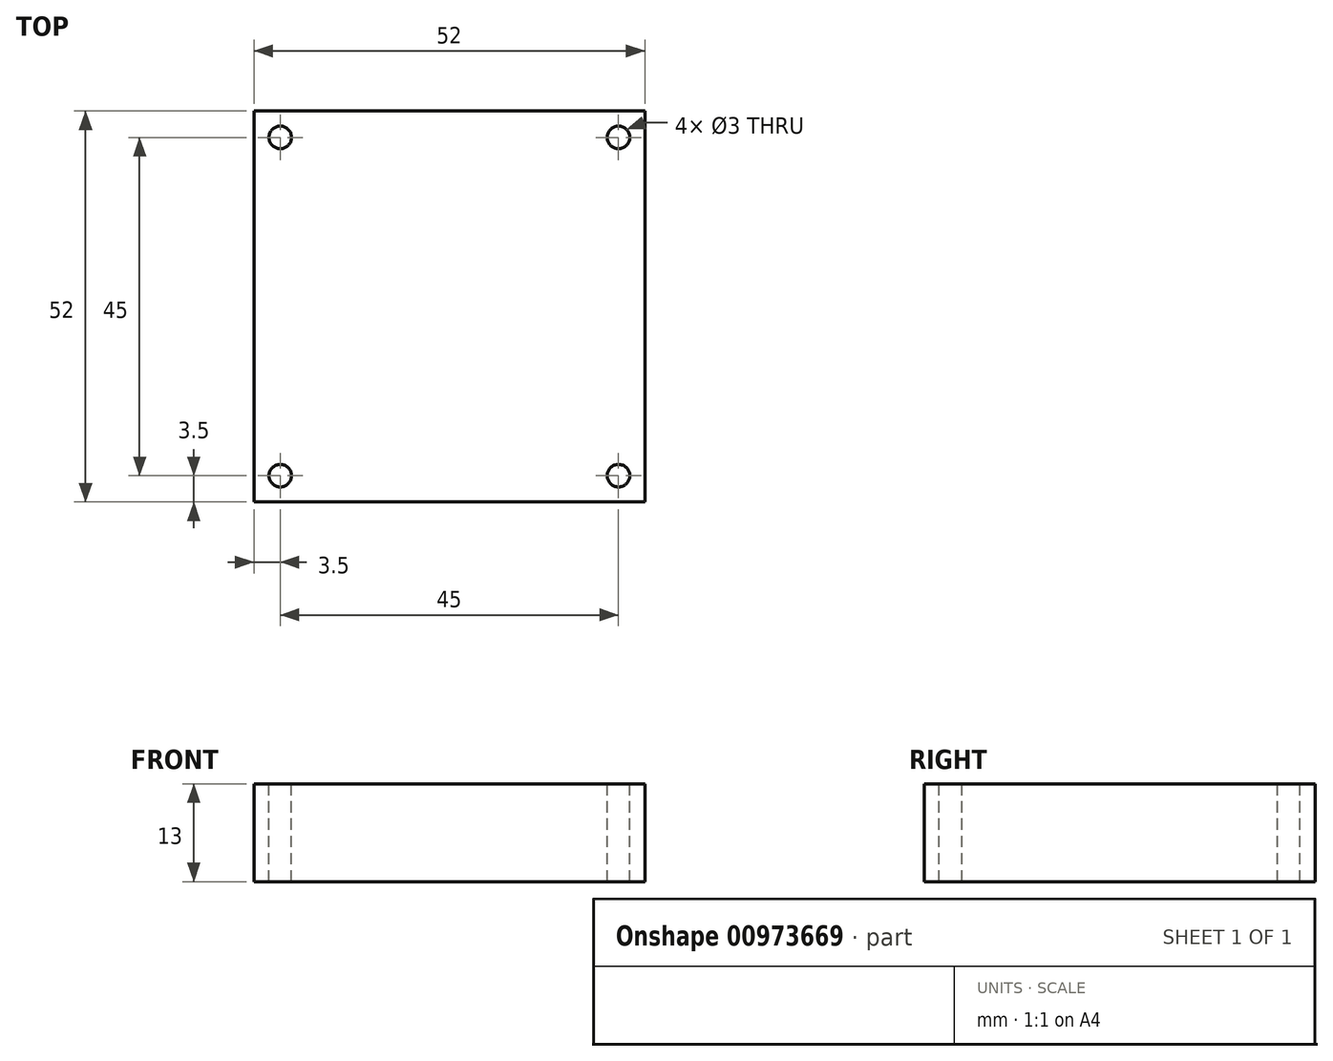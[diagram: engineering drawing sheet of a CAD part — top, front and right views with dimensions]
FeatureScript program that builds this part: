
annotation { "Feature Type Name" : "Feature", "Feature Type Description" : "" }
export const myFeature = defineFeature(function(context is Context, id is Id, definition is map)
    precondition{}
    {
        {
            var Q0;
            Q0=qCreatedBy(makeId("Top.planeOp"),FACE);
            var sketch = newSketch(context, id + "F0", { "sketchPlane" : qUnion([Q0])});
            skLineSegment(sketch, "E0.bottom", {"start": v(-26, 26) * mm, "end": v(26, 26) * mm});
            skLineSegment(sketch, "E0.top", {"start": v(-26, -26) * mm, "end": v(26, -26) * mm});
            skLineSegment(sketch, "E0.left", {"start": v(-26, 26) * mm, "end": v(-26, -26) * mm});
            skLineSegment(sketch, "E0.right", {"start": v(26, 26) * mm, "end": v(26, -26) * mm});
            skPoint(sketch, "E0.middle", {"position": v(0, 0) * mm});
            skSolve(sketch);
        }
        {
            var Q0;
            Q0 = qSketchRegion(id + "F0", true);
            extrude(context, id + "F1", {"entities" : qUnion([Q0]), "depth" : 13 * mm, "offsetDistance" : 25 * mm});
        }
        {
            var Q0;
            Q0=makeQuery(id+"F1.opExtrude","CAP_FACE",FACE,{"disambiguationData":[OSD([sQuery(id+"F0.wireOp",EDGE,"E0.bottom"),sQuery(id+"F0.wireOp",EDGE,"E0.top"),sQuery(id+"F0.wireOp",EDGE,"E0.left"),sQuery(id+"F0.wireOp",EDGE,"E0.right")])],"isStart":false});
            var sketch = newSketch(context, id + "F2", { "sketchPlane" : qUnion([Q0])});
            skCircle(sketch, "E1", {"center": v(-22.5, 22.5) * mm, "radius": 1.5 * mm});
            skCircle(sketch, "E2", {"center": v(22.5, 22.5) * mm, "radius": 1.5 * mm});
            skCircle(sketch, "E3", {"center": v(-22.5, -22.5) * mm, "radius": 1.5 * mm});
            skCircle(sketch, "E4", {"center": v(22.5, -22.5) * mm, "radius": 1.5 * mm});
            skLineSegment(sketch, "E5", {"start": v(-22.5, 22.5) * mm, "end": v(22.5, 22.5) * mm, "construction": true});
            skLineSegment(sketch, "E6", {"start": v(22.5, 22.5) * mm, "end": v(22.5, -22.5) * mm, "construction": true});
            skLineSegment(sketch, "E7", {"start": v(-22.5, -22.5) * mm, "end": v(22.5, -22.5) * mm, "construction": true});
            skLineSegment(sketch, "E8", {"start": v(-22.5, -22.5) * mm, "end": v(-22.5, 22.5) * mm, "construction": true});
            skLineSegment(sketch, "E9", {"start": v(-22.5, 22.5) * mm, "end": v(22.5, -22.5) * mm, "construction": true});
            skSolve(sketch);
        }
        {
            var Q0;
            Q0=makeQuery(id+"F2.imprint","IMPRINT",FACE,{"disambiguationData":[TD([[makeQuery(id+"F2.imprint","IMPRINT",EDGE,{"derivedFrom":sQuery(id+"F2.wireOp",EDGE,"E3")}),1.0]])]});
            var Q1;
            Q1=makeQuery(id+"F2.imprint","IMPRINT",FACE,{"disambiguationData":[TD([[makeQuery(id+"F2.imprint","IMPRINT",EDGE,{"derivedFrom":sQuery(id+"F2.wireOp",EDGE,"E4")}),1.0]])]});
            var Q2;
            Q2=makeQuery(id+"F2.imprint","IMPRINT",FACE,{"disambiguationData":[TD([[makeQuery(id+"F2.imprint","IMPRINT",EDGE,{"derivedFrom":sQuery(id+"F2.wireOp",EDGE,"E2")}),1.0]])]});
            var Q3;
            Q3=makeQuery(id+"F2.imprint","IMPRINT",FACE,{"disambiguationData":[TD([[makeQuery(id+"F2.imprint","IMPRINT",EDGE,{"derivedFrom":sQuery(id+"F2.wireOp",EDGE,"E1")}),1.0]])]});
            var Q4;
            Q4=sQuery(id+"F2.wireOp",EDGE,"E2");
            var Q5;
            Q5=sQuery(id+"F2.wireOp",EDGE,"E1");
            var Q6;
            Q6=sQuery(id+"F2.wireOp",EDGE,"E3");
            var Q7;
            Q7=sQuery(id+"F2.wireOp",EDGE,"E4");
            extrude(context, id + "F3", {"entities" : qUnion([Q0, Q1, Q2, Q3]), "operationType" : NewBodyOperationType.REMOVE, "surfaceEntities" : qUnion([Q4, Q5, Q6, Q7]), "endBound" : BoundingType.THROUGH_ALL, "oppositeDirection" : true, "depth" : 25 * mm, "offsetDistance" : 25 * mm});
        }
    });
